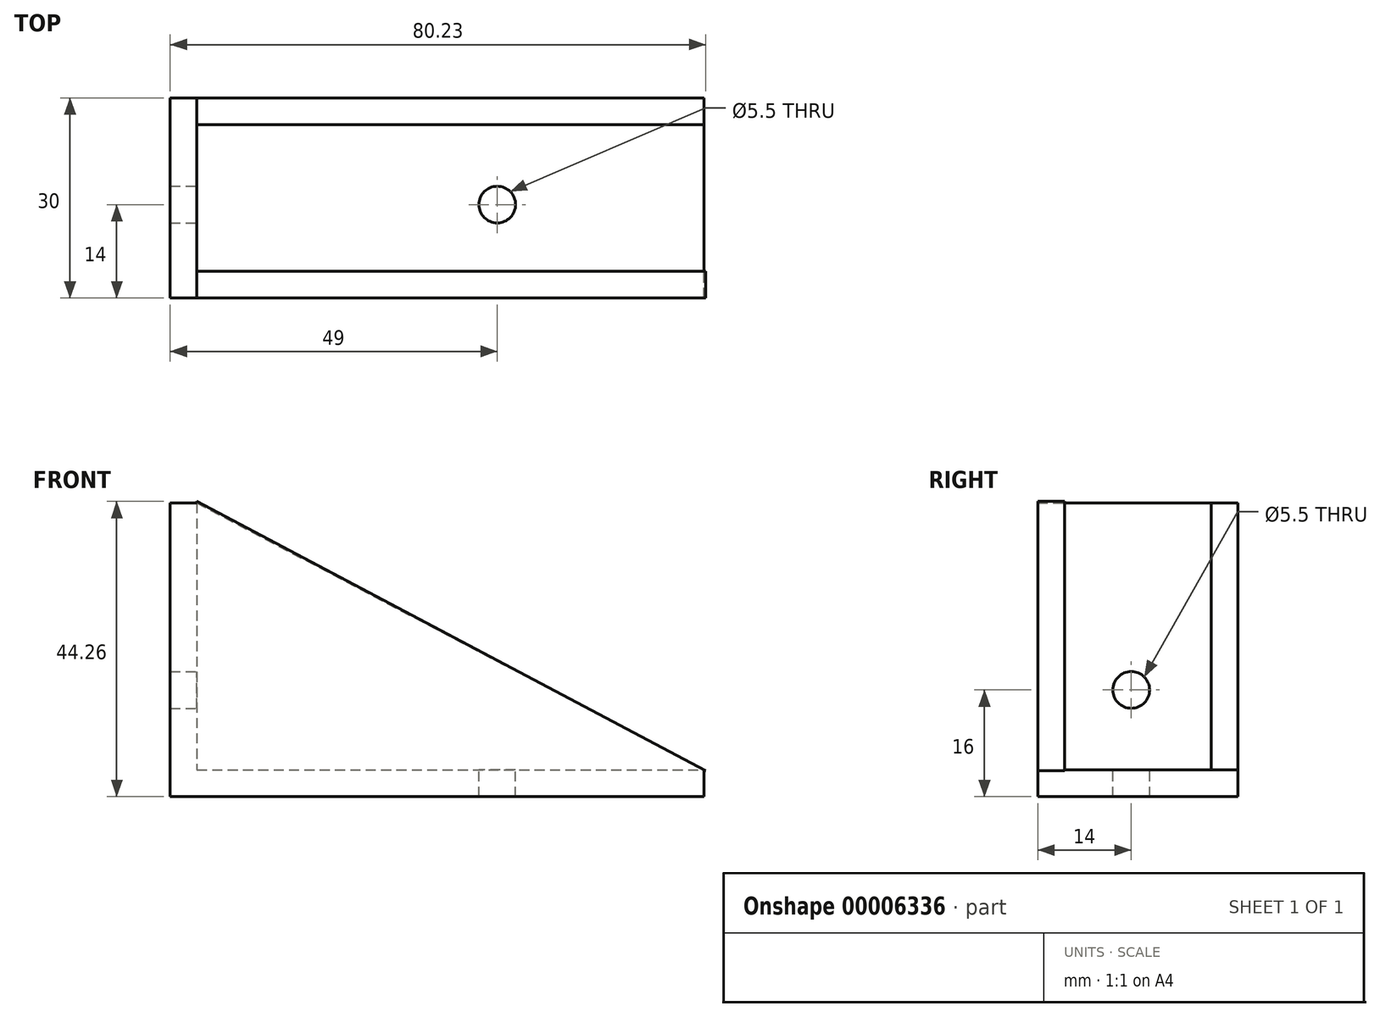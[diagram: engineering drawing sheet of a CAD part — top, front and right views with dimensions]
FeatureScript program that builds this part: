
annotation { "Feature Type Name" : "Feature", "Feature Type Description" : "" }
export const myFeature = defineFeature(function(context is Context, id is Id, definition is map)
    precondition{}
    {
        {
            var Q0;
            Q0=qCreatedBy(makeId("Top.planeOp"),FACE);
            var sketch = newSketch(context, id + "F0", { "sketchPlane" : qUnion([Q0])});
            skLineSegment(sketch, "E0.bottom", {"start": v(0, 0) * mm, "end": v(80, 0) * mm});
            skLineSegment(sketch, "E0.top", {"start": v(0, 30) * mm, "end": v(80, 30) * mm});
            skLineSegment(sketch, "E0.left", {"start": v(0, 0) * mm, "end": v(0, 30) * mm});
            skLineSegment(sketch, "E0.right", {"start": v(80, 0) * mm, "end": v(80, 30) * mm});
            skSolve(sketch);
        }
        {
            var Q0;
            Q0=makeQuery(id+"F0.imprint","IMPRINT",FACE,{"disambiguationData":[TD([[makeQuery(id+"F0.imprint","IMPRINT",EDGE,{"derivedFrom":sQuery(id+"F0.wireOp",EDGE,"E0.bottom")}),1.0]])]});
            extrude(context, id + "F1", {"entities" : qUnion([Q0]), "depth" : 4 * mm});
        }
        {
            var Q0;
            Q0=makeQuery(id+"F1.opExtrude","CAP_FACE",FACE,{"disambiguationData":[OSD([sQuery(id+"F0.wireOp",EDGE,"E0.bottom"),sQuery(id+"F0.wireOp",EDGE,"E0.top"),sQuery(id+"F0.wireOp",EDGE,"E0.left"),sQuery(id+"F0.wireOp",EDGE,"E0.right")])],"isStart":false});
            var sketch = newSketch(context, id + "F2", { "sketchPlane" : qUnion([Q0])});
            skLineSegment(sketch, "E1.bottom", {"start": v(0, 0) * mm, "end": v(4, 0) * mm});
            skLineSegment(sketch, "E1.top", {"start": v(0, 30) * mm, "end": v(4, 30) * mm});
            skLineSegment(sketch, "E1.left", {"start": v(0, 0) * mm, "end": v(0, 30) * mm});
            skLineSegment(sketch, "E1.right", {"start": v(4, 0) * mm, "end": v(4, 30) * mm});
            skSolve(sketch);
        }
        {
            var Q0;
            Q0=makeQuery(id+"F2.imprint","IMPRINT",FACE,{"disambiguationData":[TD([[makeQuery(id+"F2.imprint","IMPRINT",EDGE,{"derivedFrom":sQuery(id+"F2.wireOp",EDGE,"E1.bottom")}),1.0]])]});
            extrude(context, id + "F3", {"entities" : qUnion([Q0]), "operationType" : NewBodyOperationType.ADD, "depth" : 40 * mm});
        }
        {
            var Q0;
            Q0=qCreatedBy(makeId("Front.planeOp"),FACE);
            var sketch = newSketch(context, id + "F4", { "sketchPlane" : qUnion([Q0])});
            skLineSegment(sketch, "E2", {"start": v(4, 44.26) * mm, "end": v(80.23, 3.91) * mm});
            skLineSegment(sketch, "E3", {"start": v(80.23, 3.91) * mm, "end": v(2.15, 3.91) * mm});
            skLineSegment(sketch, "E4", {"start": v(2.15, 3.91) * mm, "end": v(4, 44.26) * mm});
            skSolve(sketch);
        }
        {
            var Q0;
            Q0=makeQuery(id+"F4.imprint","IMPRINT",FACE,{"disambiguationData":[TD([[makeQuery(id+"F4.imprint","IMPRINT",EDGE,{"derivedFrom":sQuery(id+"F4.wireOp",EDGE,"E2")}),-1.0]])]});
            extrude(context, id + "F5", {"entities" : qUnion([Q0]), "operationType" : NewBodyOperationType.ADD, "oppositeDirection" : true, "depth" : 4 * mm});
        }
        {
            var Q0;
            Q0=makeQuery(id+"F3.boolean.opBoolean","MERGE",FACE,{"derivedFrom":[makeQuery(id+"F1.opExtrude","SWEPT_FACE",FACE,{"disambiguationData":[OSD([sQuery(id+"F0.wireOp",EDGE,"E0.top")])]}),makeQuery(id+"F3.opExtrude","SWEPT_FACE",FACE,{"disambiguationData":[OSD([sQuery(id+"F2.wireOp",EDGE,"E1.top")])]})]});
            var sketch = newSketch(context, id + "F6", { "sketchPlane" : qUnion([Q0])});
            skLineSegment(sketch, "E5", {"start": v(-4, 44) * mm, "end": v(-80, 4) * mm});
            skLineSegment(sketch, "E6", {"start": v(-80, 4) * mm, "end": v(-2.73, 1.96) * mm});
            skLineSegment(sketch, "E7", {"start": v(-2.73, 1.96) * mm, "end": v(-4, 44) * mm});
            skSolve(sketch);
        }
        {
            var Q0;
            Q0=makeQuery(id+"F6.imprint","IMPRINT",FACE,{"disambiguationData":[TD([[makeQuery(id+"F6.imprint","IMPRINT",EDGE,{"derivedFrom":sQuery(id+"F6.wireOp",EDGE,"E5")}),1.0]])]});
            var Q1;
            Q1=makeQuery(id+"F6.imprint","IMPRINT",FACE,{"disambiguationData":[TD([[makeQuery(id+"F6.imprint","IMPRINT",EDGE,{"derivedFrom":sQuery(id+"F6.wireOp",EDGE,"E6")}),-1.0]])]});
            extrude(context, id + "F7", {"entities" : qUnion([Q0, Q1]), "operationType" : NewBodyOperationType.ADD, "oppositeDirection" : true, "depth" : 4 * mm});
        }
        {
            var Q0;
            Q0=makeQuery(id+"F1.opExtrude","CAP_FACE",FACE,{"disambiguationData":[OSD([sQuery(id+"F0.wireOp",EDGE,"E0.bottom"),sQuery(id+"F0.wireOp",EDGE,"E0.top"),sQuery(id+"F0.wireOp",EDGE,"E0.left"),sQuery(id+"F0.wireOp",EDGE,"E0.right")])],"isStart":false});
            var sketch = newSketch(context, id + "F8", { "sketchPlane" : qUnion([Q0])});
            skCircle(sketch, "E8", {"center": v(49, 14) * mm, "radius": 2.75 * mm});
            skSolve(sketch);
        }
        {
            var Q0;
            Q0=makeQuery(id+"F8.imprint","IMPRINT",FACE,{"disambiguationData":[TD([[makeQuery(id+"F8.imprint","IMPRINT",EDGE,{"derivedFrom":sQuery(id+"F8.wireOp",EDGE,"E8")}),1.0]])]});
            extrude(context, id + "F9", {"entities" : qUnion([Q0]), "operationType" : NewBodyOperationType.REMOVE, "oppositeDirection" : true, "depth" : 25 * mm});
        }
        {
            var Q0;
            Q0=makeQuery(id+"F3.opExtrude","SWEPT_FACE",FACE,{"disambiguationData":[OSD([sQuery(id+"F2.wireOp",EDGE,"E1.right")])]});
            var sketch = newSketch(context, id + "F10", { "sketchPlane" : qUnion([Q0])});
            skCircle(sketch, "E9", {"center": v(14, 16) * mm, "radius": 2.75 * mm});
            skSolve(sketch);
        }
        {
            var Q0;
            Q0=makeQuery(id+"F10.imprint","IMPRINT",FACE,{"disambiguationData":[TD([[makeQuery(id+"F10.imprint","IMPRINT",EDGE,{"derivedFrom":sQuery(id+"F10.wireOp",EDGE,"E9")}),1.0]])]});
            extrude(context, id + "F11", {"entities" : qUnion([Q0]), "operationType" : NewBodyOperationType.REMOVE, "oppositeDirection" : true, "depth" : 25 * mm});
        }
    });
